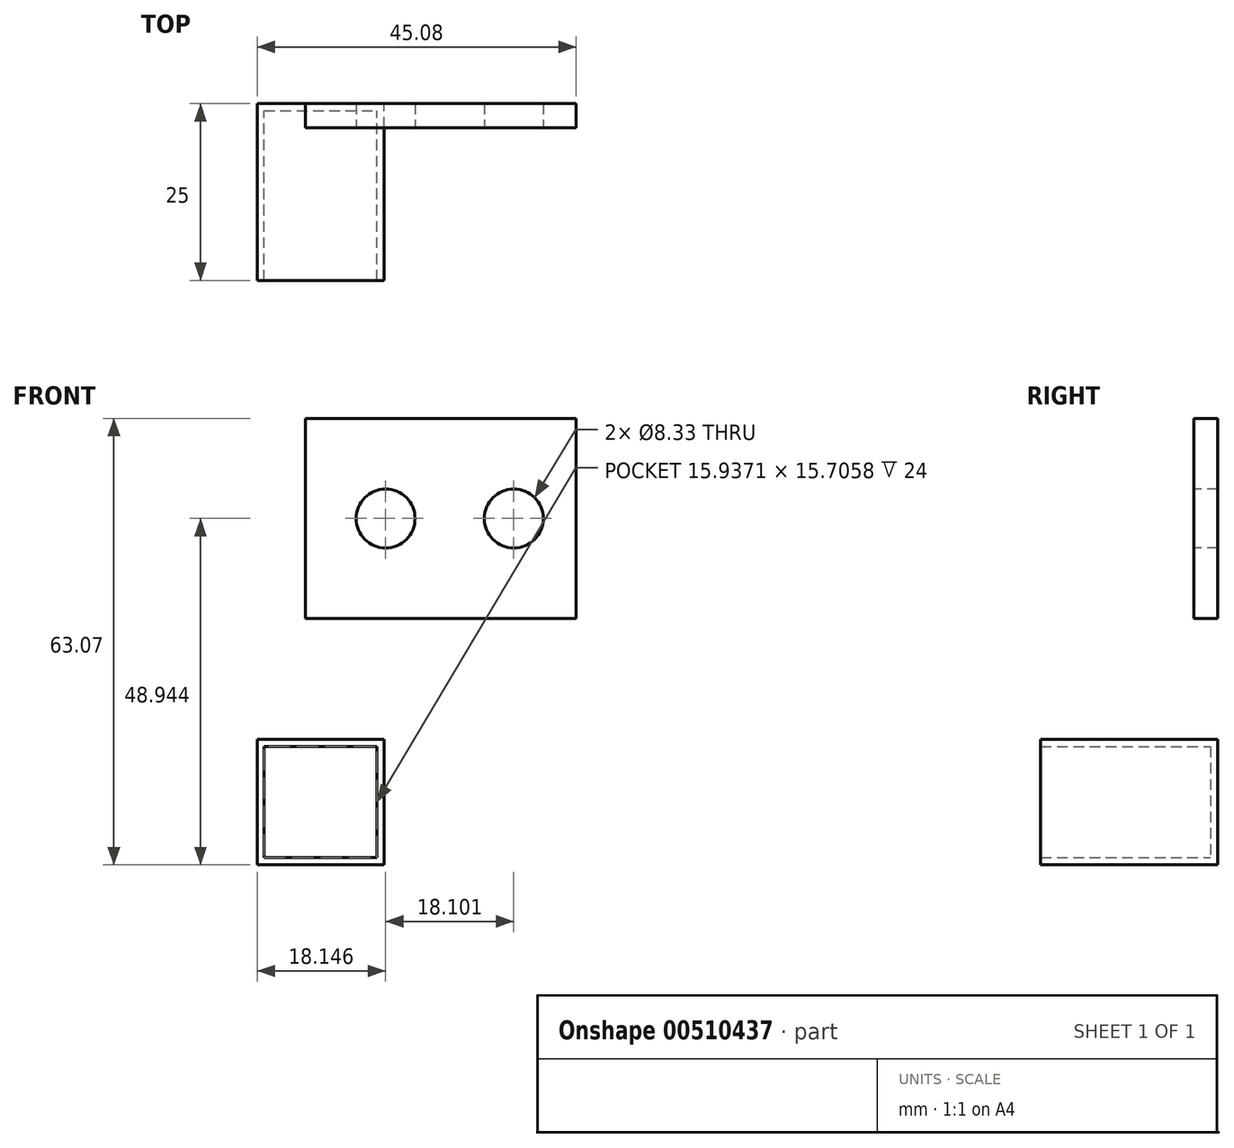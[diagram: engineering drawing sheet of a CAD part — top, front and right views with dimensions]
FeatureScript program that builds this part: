
annotation { "Feature Type Name" : "Feature", "Feature Type Description" : "" }
export const myFeature = defineFeature(function(context is Context, id is Id, definition is map)
    precondition{}
    {
        {
            var Q0;
            Q0=qCreatedBy(makeId("Front.planeOp"),FACE);
            var sketch = newSketch(context, id + "F0", { "sketchPlane" : qUnion([Q0])});
            skLineSegment(sketch, "E0.bottom", {"start": v(-131.42, 60.2) * mm, "end": v(-93.18, 60.2) * mm});
            skLineSegment(sketch, "E0.top", {"start": v(-131.42, 31.96) * mm, "end": v(-93.18, 31.96) * mm});
            skLineSegment(sketch, "E0.left", {"start": v(-131.42, 60.2) * mm, "end": v(-131.42, 31.96) * mm});
            skLineSegment(sketch, "E0.right", {"start": v(-93.18, 60.2) * mm, "end": v(-93.18, 31.96) * mm});
            skPoint(sketch, "E1", {"position": v(-131.42, 46.08) * mm});
            skPoint(sketch, "E2", {"position": v(-112.3, 31.96) * mm});
            skSolve(sketch);
        }
        {
            var Q0;
            Q0=makeQuery(id+"F0.imprint","IMPRINT",FACE,{"disambiguationData":[TD([[makeQuery(id+"F0.imprint","IMPRINT",EDGE,{"derivedFrom":sQuery(id+"F0.wireOp",EDGE,"E0.bottom")}),-1.0]])]});
            extrude(context, id + "F1", {"entities" : qUnion([Q0]), "depth" : 3.4 * mm});
        }
        {
            var Q0;
            Q0=makeQuery(id+"F1.opExtrude","CAP_FACE",FACE,{"disambiguationData":[OSD([sQuery(id+"F0.wireOp",EDGE,"E0.bottom"),sQuery(id+"F0.wireOp",EDGE,"E0.top"),sQuery(id+"F0.wireOp",EDGE,"E0.left"),sQuery(id+"F0.wireOp",EDGE,"E0.right")])],"isStart":false});
            var sketch = newSketch(context, id + "F2", { "sketchPlane" : qUnion([Q0])});
            skCircle(sketch, "E3", {"center": v(-120.11, 46.08) * mm, "radius": 4.17 * mm});
            skCircle(sketch, "E4", {"center": v(-102.01, 46.08) * mm, "radius": 4.17 * mm});
            skSolve(sketch);
        }
        {
            var Q0;
            Q0 = qSketchRegion(id + "F2", true);
            extrude(context, id + "F3", {"entities" : qUnion([Q0]), "operationType" : NewBodyOperationType.REMOVE, "oppositeDirection" : true, "depth" : 25 * mm});
        }
        {
            var Q0;
            Q0=qCreatedBy(makeId("Front.planeOp"),FACE);
            var sketch = newSketch(context, id + "F4", { "sketchPlane" : qUnion([Q0])});
            skLineSegment(sketch, "E5.bottom", {"start": v(-138.26, 14.84) * mm, "end": v(-120.32, 14.84) * mm});
            skLineSegment(sketch, "E5.top", {"start": v(-138.26, -2.86) * mm, "end": v(-120.32, -2.86) * mm});
            skLineSegment(sketch, "E5.left", {"start": v(-138.26, 14.84) * mm, "end": v(-138.26, -2.86) * mm});
            skLineSegment(sketch, "E5.right", {"start": v(-120.32, 14.84) * mm, "end": v(-120.32, -2.86) * mm});
            skSolve(sketch);
        }
        {
            var Q0;
            Q0 = qSketchRegion(id + "F4", true);
            extrude(context, id + "F5", {"entities" : qUnion([Q0]), "depth" : 25 * mm});
        }
        {
            var Q0;
            Q0=makeQuery(id+"F5.opExtrude","CAP_FACE",FACE,{"disambiguationData":[OSD([sQuery(id+"F4.wireOp",EDGE,"E5.bottom"),sQuery(id+"F4.wireOp",EDGE,"E5.top"),sQuery(id+"F4.wireOp",EDGE,"E5.left"),sQuery(id+"F4.wireOp",EDGE,"E5.right")])],"isStart":false});
            shell(context, id + "F6", {"entities" : qUnion([Q0]), "thickness" : 1 * mm});
        }
    });
